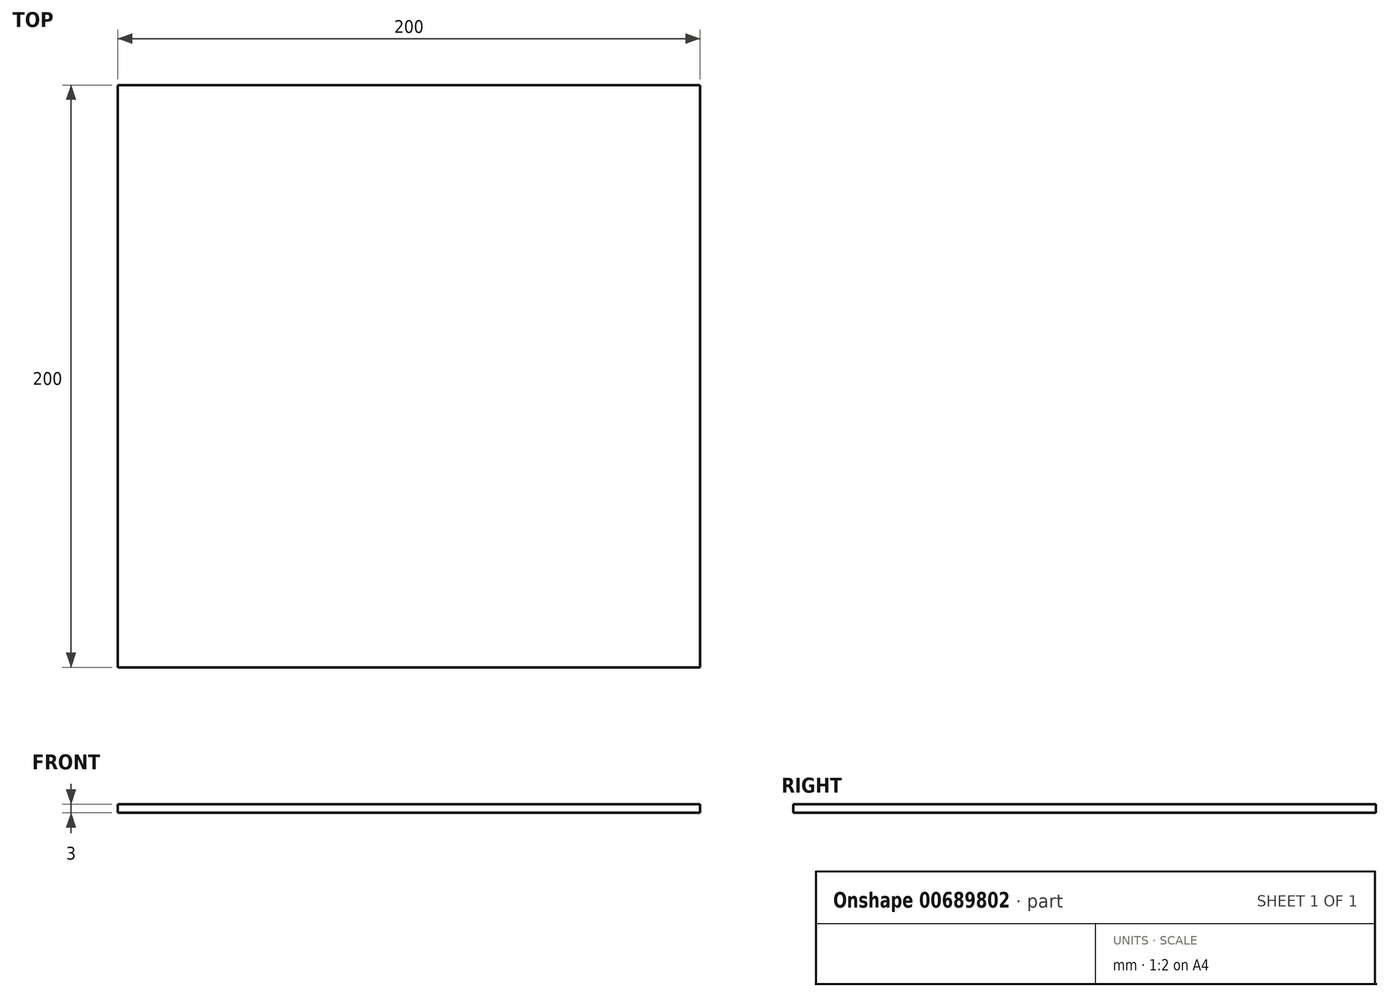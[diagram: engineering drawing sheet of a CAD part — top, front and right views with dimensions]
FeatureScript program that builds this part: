
annotation { "Feature Type Name" : "Feature", "Feature Type Description" : "" }
export const myFeature = defineFeature(function(context is Context, id is Id, definition is map)
    precondition{}
    {
        {
            var Q0;
            Q0=qCreatedBy(makeId("Top.planeOp"),FACE);
            var sketch = newSketch(context, id + "F0", { "sketchPlane" : qUnion([Q0])});
            skLineSegment(sketch, "E0.bottom", {"start": v(0, 0) * mm, "end": v(200, 0) * mm});
            skLineSegment(sketch, "E0.top", {"start": v(0, 200) * mm, "end": v(200, 200) * mm});
            skLineSegment(sketch, "E0.left", {"start": v(0, 0) * mm, "end": v(0, 200) * mm});
            skLineSegment(sketch, "E0.right", {"start": v(200, 0) * mm, "end": v(200, 200) * mm});
            skSolve(sketch);
        }
        {
            var Q0;
            Q0=makeQuery(id+"F0.imprint","IMPRINT",FACE,{"disambiguationData":[TD([[makeQuery(id+"F0.imprint","IMPRINT",EDGE,{"derivedFrom":sQuery(id+"F0.wireOp",EDGE,"E0.bottom")}),1.0]])]});
            extrude(context, id + "F1", {"entities" : qUnion([Q0]), "depth" : 3 * mm, "offsetDistance" : 25 * mm});
        }
    });
